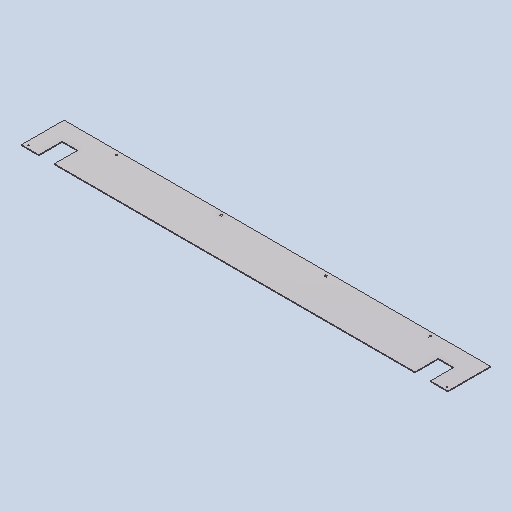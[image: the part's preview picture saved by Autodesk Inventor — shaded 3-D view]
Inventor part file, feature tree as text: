
AUTODESK INVENTOR PART (.ipt)
format: ipt  version: 2025 (Build 290162010, 162A)  size: 205,824 bytes
history: native  units: mm
features: sketch x3, hole x2, extrude x1, other x1
ambient origin geometry x8: Origin, YZ Plane, XZ Plane, XY Plane, X Axis, Y Axis, Z Axis, Center Point
bodies: Volumenkörper1 (feature_tree)
feature tree (7):
  hole  "Bohrung1"  [1 undecoded]
  extrude  "Extrusion1"  Depth=60.0mm
  hole  "Bohrung2"  [1 undecoded]
  sketch  "Skizze1"  dims[d2=270.0mm d3=10.0mm]
  sketch  "Skizze2"  dims[d4=4.3mm d5=6.0mm d6=9.4mm d7=2.0mm d8=90.0deg d9=8.0mm d10=20.594885mm d12=60.0mm]
  sketch  "Skizze3"  dims[d14=40.0mm d15=465.0mm d16=50.0mm d17=0.0mm d18=0.0mm d19=8.0mm d20=10.0mm d21=8.0mm d22=10.0mm d23=3.2mm d24=6.0mm d25=6.3mm d26=2.0mm d27=90.0deg d28=8.0mm d29=20.594885mm]
  other  "item_47308_blech-al-2mm-naturfarben_110_1100_high_1_1:1"
note: 2 required parameter values undecoded (feature->parameter linkage not recoverable at this tier; creation-order binding heuristic only, values carry confidence <= 0.55)
